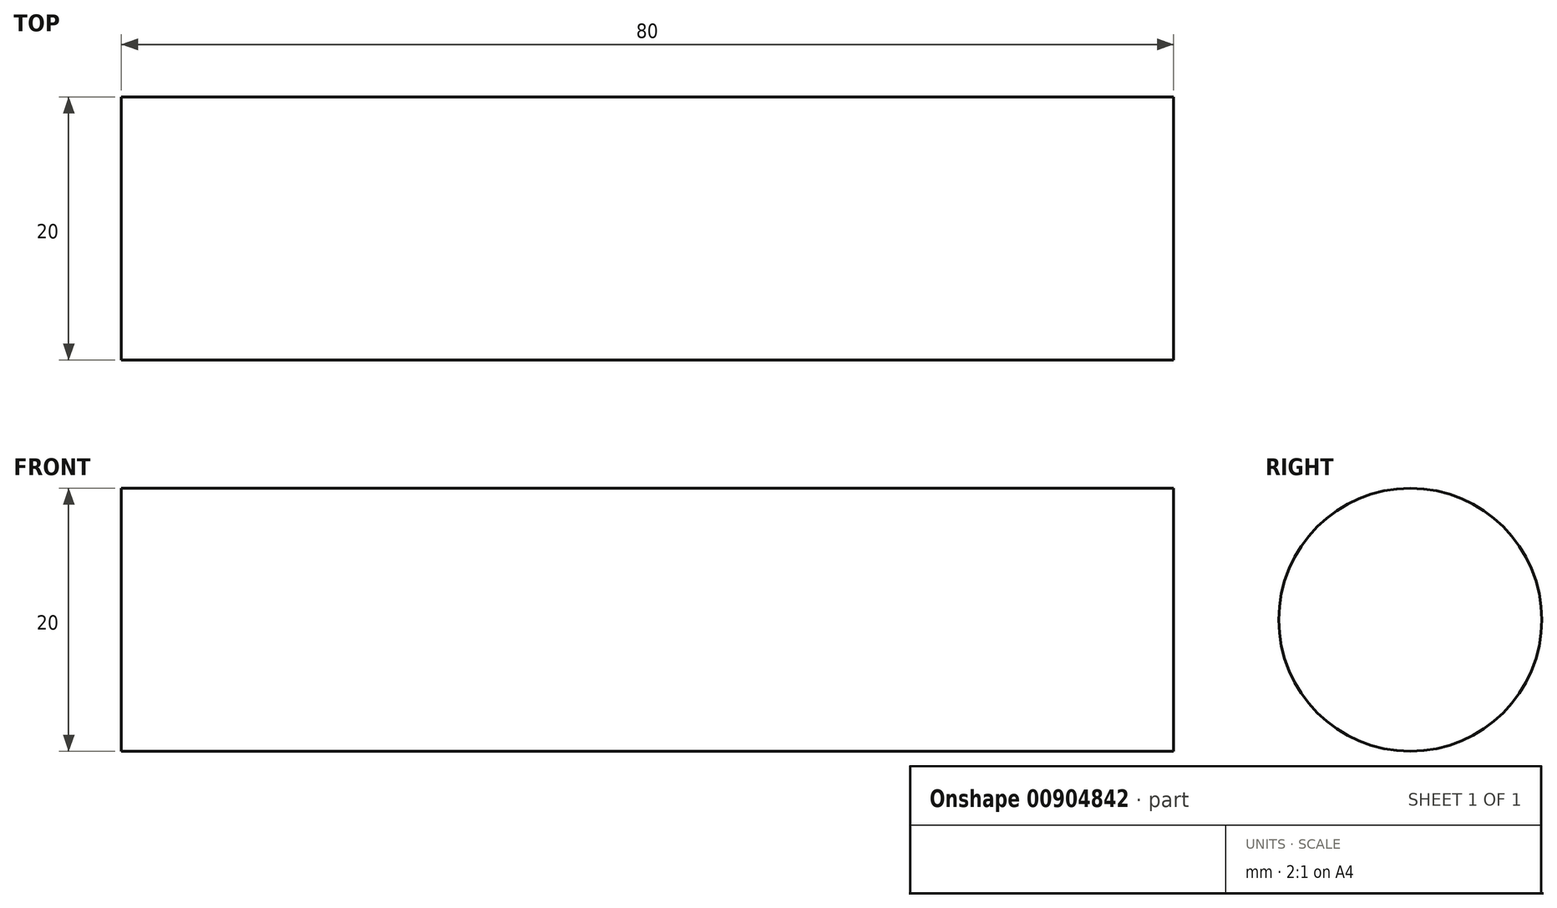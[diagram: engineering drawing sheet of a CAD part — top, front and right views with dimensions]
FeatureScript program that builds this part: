
annotation { "Feature Type Name" : "Feature", "Feature Type Description" : "" }
export const myFeature = defineFeature(function(context is Context, id is Id, definition is map)
    precondition{}
    {
        {
            var Q0;
            Q0=qCreatedBy(makeId("Right.planeOp"),FACE);
            var sketch = newSketch(context, id + "F0", { "sketchPlane" : qUnion([Q0])});
            skCircle(sketch, "E0", {"center": v(0, 0) * mm, "radius": 10 * mm});
            skSolve(sketch);
        }
        {
            var Q0;
            Q0=makeQuery(id+"F0.imprint","IMPRINT",FACE,{"disambiguationData":[TD([[makeQuery(id+"F0.imprint","IMPRINT",EDGE,{"derivedFrom":sQuery(id+"F0.wireOp",EDGE,"E0")}),1.0]])]});
            extrude(context, id + "F1", {"entities" : qUnion([Q0]), "depth" : 80 * mm, "offsetDistance" : 25 * mm});
        }
    });
